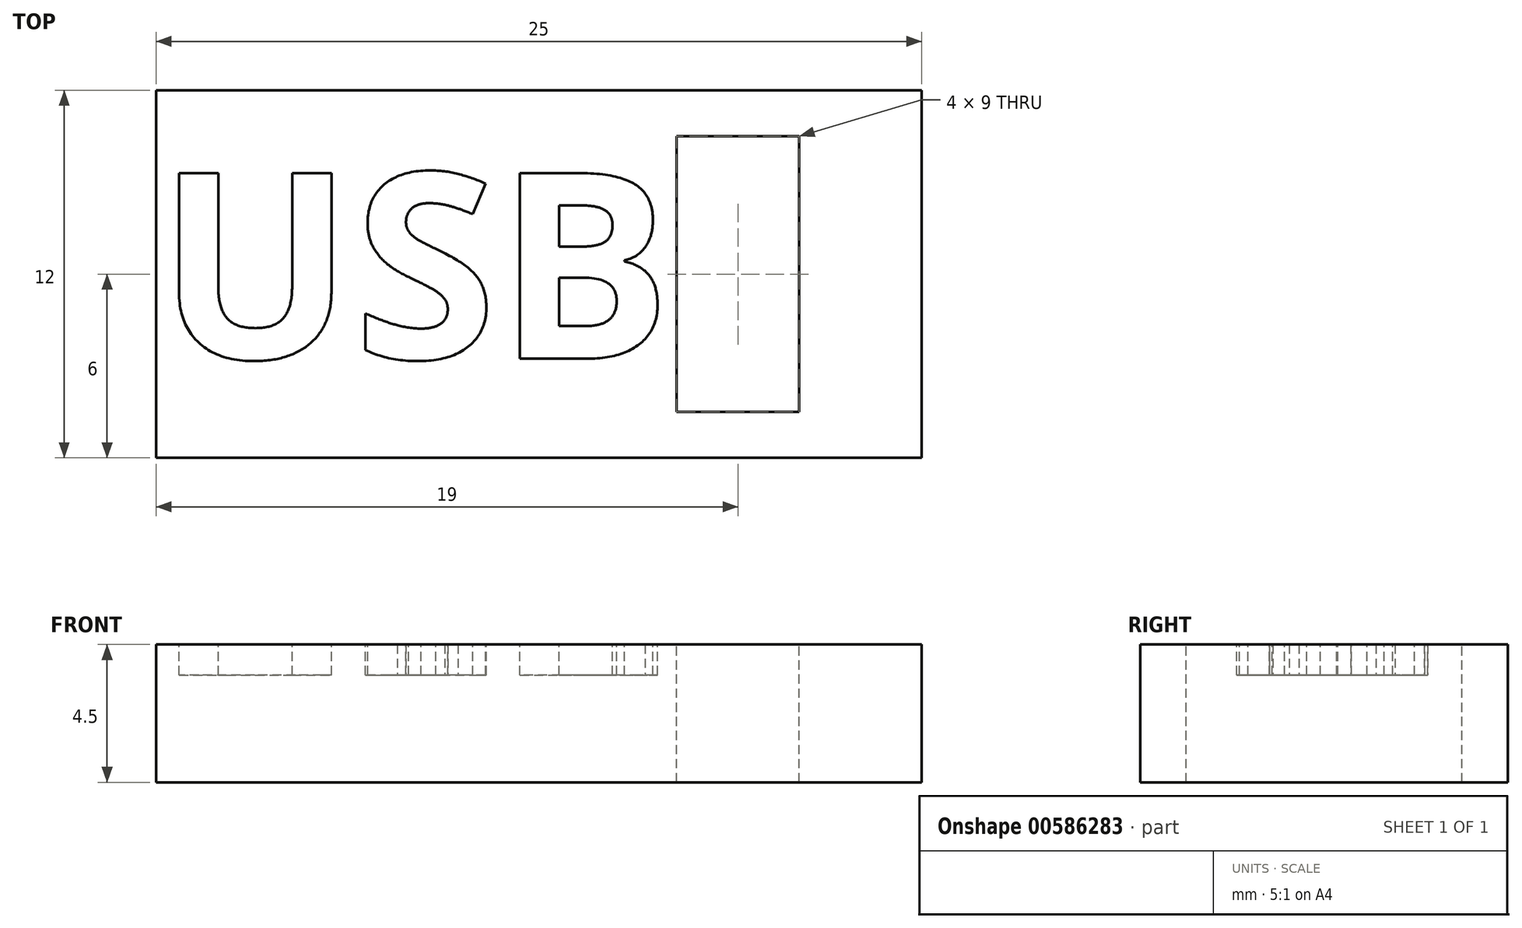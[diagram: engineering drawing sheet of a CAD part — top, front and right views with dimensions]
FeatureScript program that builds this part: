
annotation { "Feature Type Name" : "Feature", "Feature Type Description" : "" }
export const myFeature = defineFeature(function(context is Context, id is Id, definition is map)
    precondition{}
    {
        {
            var Q0;
            Q0=qCreatedBy(makeId("Top.planeOp"),FACE);
            var sketch = newSketch(context, id + "F0", { "sketchPlane" : qUnion([Q0])});
            skLineSegment(sketch, "E0.bottom", {"start": v(12.5, 6) * mm, "end": v(-12.5, 6) * mm});
            skLineSegment(sketch, "E0.top", {"start": v(12.5, -6) * mm, "end": v(-12.5, -6) * mm});
            skLineSegment(sketch, "E0.left", {"start": v(12.5, 6) * mm, "end": v(12.5, -6) * mm});
            skLineSegment(sketch, "E0.right", {"start": v(-12.5, 6) * mm, "end": v(-12.5, -6) * mm});
            skPoint(sketch, "E0.middle", {"position": v(0, 0) * mm});
            skSolve(sketch);
        }
        {
            var Q0;
            Q0=makeQuery(id+"F0.imprint","IMPRINT",FACE,{"disambiguationData":[TD([[makeQuery(id+"F0.imprint","IMPRINT",EDGE,{"derivedFrom":sQuery(id+"F0.wireOp",EDGE,"E0.bottom")}),1.0]])]});
            extrude(context, id + "F1", {"entities" : qUnion([Q0]), "depth" : 4.5 * mm, "offsetDistance" : 25 * mm});
        }
        {
            var Q0;
            Q0=makeQuery(id+"F1.opExtrude","CAP_FACE",FACE,{"disambiguationData":[OSD([sQuery(id+"F0.wireOp",EDGE,"E0.bottom"),sQuery(id+"F0.wireOp",EDGE,"E0.top"),sQuery(id+"F0.wireOp",EDGE,"E0.left"),sQuery(id+"F0.wireOp",EDGE,"E0.right")])],"isStart":false});
            var sketch = newSketch(context, id + "F2", { "sketchPlane" : qUnion([Q0])});
            skLineSegment(sketch, "E1.bottom", {"start": v(8.5, 4.5) * mm, "end": v(4.5, 4.5) * mm});
            skLineSegment(sketch, "E1.top", {"start": v(8.5, -4.5) * mm, "end": v(4.5, -4.5) * mm});
            skLineSegment(sketch, "E1.left", {"start": v(8.5, 4.5) * mm, "end": v(8.5, -4.5) * mm});
            skLineSegment(sketch, "E1.right", {"start": v(4.5, 4.5) * mm, "end": v(4.5, -4.5) * mm});
            skPoint(sketch, "E1.middle", {"position": v(6.5, 0) * mm});
            skSolve(sketch);
        }
        {
            var Q0;
            Q0=makeQuery(id+"F2.imprint","IMPRINT",FACE,{"disambiguationData":[TD([[makeQuery(id+"F2.imprint","IMPRINT",EDGE,{"derivedFrom":sQuery(id+"F2.wireOp",EDGE,"E1.bottom")}),1.0]])]});
            extrude(context, id + "F3", {"entities" : qUnion([Q0]), "operationType" : NewBodyOperationType.REMOVE, "oppositeDirection" : true, "depth" : 25 * mm, "offsetDistance" : 25 * mm});
        }
        {
            var Q0;
            Q0=makeQuery(id+"F1.opExtrude","CAP_FACE",FACE,{"disambiguationData":[OSD([sQuery(id+"F0.wireOp",EDGE,"E0.bottom"),sQuery(id+"F0.wireOp",EDGE,"E0.top"),sQuery(id+"F0.wireOp",EDGE,"E0.left"),sQuery(id+"F0.wireOp",EDGE,"E0.right")])],"isStart":false});
            var sketch = newSketch(context, id + "F4", { "sketchPlane" : qUnion([Q0])});
            skText(sketch, "E2", { "text": "USB", "fontName": "OpenSans-Bold.ttf"});
            const initialGuessF4  = {"E2": [-0.01247, -0.00276, 1, 0, 0.00611]};
            skSetInitialGuess(sketch, initialGuessF4);
            skSolve(sketch);
        }
        {
            var Q0;
            Q0=makeQuery(id+"F4.imprint","IMPRINT",FACE,{"disambiguationData":[TD([[makeQuery(id+"F4.imprint","IMPRINT",EDGE,{"derivedFrom":sQuery(id+"F4.wireOp",EDGE,"E2.sketch_text.stroke-0")}),-1.0]])]});
            var Q1;
            Q1=makeQuery(id+"F4.imprint","IMPRINT",FACE,{"disambiguationData":[TD([[makeQuery(id+"F4.imprint","IMPRINT",EDGE,{"derivedFrom":sQuery(id+"F4.wireOp",EDGE,"E2.sketch_text.stroke-15")}),-1.0]])]});
            var Q2;
            Q2=makeQuery(id+"F4.imprint","IMPRINT",FACE,{"disambiguationData":[TD([[makeQuery(id+"F4.imprint","IMPRINT",EDGE,{"derivedFrom":sQuery(id+"F4.wireOp",EDGE,"E2.sketch_text.stroke-43")}),-1.0]])]});
            extrude(context, id + "F5", {"entities" : qUnion([Q0, Q1, Q2]), "operationType" : NewBodyOperationType.REMOVE, "oppositeDirection" : true, "depth" : 1 * mm, "offsetDistance" : 25 * mm});
        }
    });
